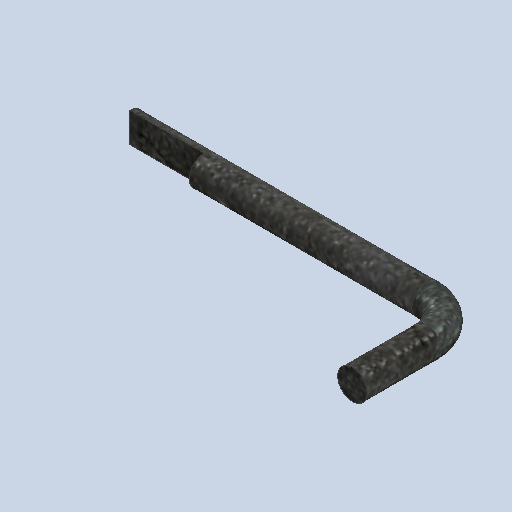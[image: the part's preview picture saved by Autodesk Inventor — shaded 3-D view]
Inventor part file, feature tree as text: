
AUTODESK INVENTOR PART (.ipt)
format: ipt  version: 2024.3 (Build 283343000, 343)  size: 261,632 bytes
history: native  units: mm
features: sketch x4, extrude x3, projected_geometry x2, revolve x1
ambient origin geometry x8: Origin, YZ Plane, XZ Plane, XY Plane, X Axis, Y Axis, Z Axis, Center Point
bodies: Solid1 (feature_tree)
feature tree (10):
  extrude  "Extrusion1"  Depth=80.0mm TaperAngle=0.0deg
  revolve  "Revolution2"  Angle=90.0deg
  extrude  "Extrusion6"  Depth=20.0mm TaperAngle=0.0deg
  extrude  "Extrusion7"  [1 undecoded]
  sketch  "Sketch1"  dims[d0=8.0mm d1=80.0mm d2=0.0mm]
  sketch  "Sketch8"  dims[d13=10.0mm d15=90.0deg]
  projected_geometry  "Projected Loop3"
  sketch  "Sketch9"  dims[d16=20.0mm d17=0.0mm d18=20.0mm d19=0.0mm]
  projected_geometry  "Projected Loop4"
  sketch  "Sketch10"
note: 1 required parameter value undecoded (feature->parameter linkage not recoverable at this tier; creation-order binding heuristic only, values carry confidence <= 0.55)
